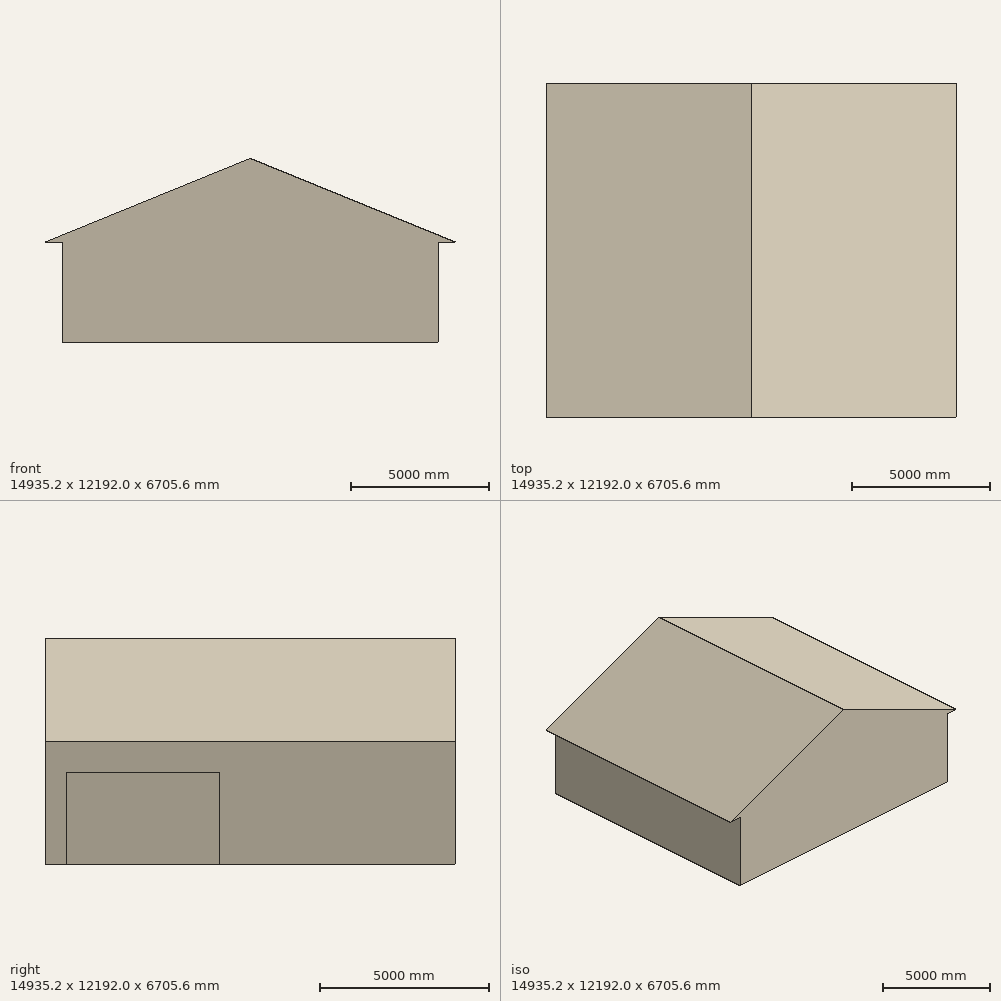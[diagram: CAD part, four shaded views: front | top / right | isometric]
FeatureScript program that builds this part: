
annotation { "Feature Type Name" : "Feature", "Feature Type Description" : "" }
export const myFeature = defineFeature(function(context is Context, id is Id, definition is map)
    precondition{}
    {
        {
            var Q0;
            Q0=qCreatedBy(makeId("Top.planeOp"),FACE);
            var sketch = newSketch(context, id + "F0", { "sketchPlane" : qUnion([Q0])});
            skLineSegment(sketch, "E0.bottom", {"start": v(6858, 6096) * mm, "end": v(-6858, 6096) * mm});
            skLineSegment(sketch, "E0.top", {"start": v(6858, -6096) * mm, "end": v(-6858, -6096) * mm});
            skLineSegment(sketch, "E0.left", {"start": v(6858, 6096) * mm, "end": v(6858, -6096) * mm});
            skLineSegment(sketch, "E0.right", {"start": v(-6858, 6096) * mm, "end": v(-6858, -6096) * mm});
            skPoint(sketch, "E0.middle", {"position": v(0, 0) * mm});
            skSolve(sketch);
        }
        {
            var Q0;
            Q0=makeQuery(id+"F0.imprint","IMPRINT",FACE,{"disambiguationData":[TD([[makeQuery(id+"F0.imprint","IMPRINT",EDGE,{"derivedFrom":sQuery(id+"F0.wireOp",EDGE,"E0.bottom")}),1.0]])]});
            extrude(context, id + "F1", {"entities" : qUnion([Q0]), "depth" : 3657.6 * mm});
        }
        {
            var Q0;
            Q0=makeQuery(id+"F1.opExtrude","SWEPT_FACE",FACE,{"disambiguationData":[OSD([sQuery(id+"F0.wireOp",EDGE,"E0.bottom")])]});
            var sketch = newSketch(context, id + "F2", { "sketchPlane" : qUnion([Q0])});
            skLineSegment(sketch, "E1", {"start": v(0, 0) * mm, "end": v(0, 2743.2) * mm});
            skPoint(sketch, "E1.endSnap0", {"position": v(0, 0) * mm});
            skLineSegment(sketch, "E2", {"start": v(0, 2743.2) * mm, "end": v(6096, 2743.2) * mm});
            skLineSegment(sketch, "E3", {"start": v(6096, 2743.2) * mm, "end": v(6096, 0) * mm});
            skSolve(sketch);
        }
        {
            var Q0;
            {var subQ0=sQuery(id+"F2.wireOp",EDGE,"E1");Q0=makeQuery(id+"F2.imprint","IMPRINT",FACE,{"disambiguationData":[TD([[makeQuery(id+"F2.imprint","IMPRINT",EDGE,{"derivedFrom":subQ0}),-1.0]])]});}
            extrude(context, id + "F3", {"entities" : qUnion([Q0]), "operationType" : NewBodyOperationType.REMOVE, "oppositeDirection" : true, "depth" : 12070.08 * mm});
        }
        {
            var Q0;
            Q0=makeQuery(id+"F1.opExtrude","SWEPT_FACE",FACE,{"disambiguationData":[OSD([sQuery(id+"F0.wireOp",EDGE,"E0.left")])]});
            var sketch = newSketch(context, id + "F4", { "sketchPlane" : qUnion([Q0])});
            skPoint(sketch, "E4.endSnap0", {"position": v(-914.4, 0) * mm});
            skLineSegment(sketch, "E5", {"start": v(-914.4, 2743.2) * mm, "end": v(-5486.4, 2743.2) * mm});
            skLineSegment(sketch, "E6", {"start": v(-5486.4, 2743.2) * mm, "end": v(-5486.4, 0) * mm});
            skLineSegment(sketch, "E7", {"start": v(-914.4, 2743.2) * mm, "end": v(-914.4, 0) * mm});
            skSolve(sketch);
        }
        {
            var Q0;
            Q0 = qSketchRegion(id + "F4", true);
            var Q1;
            Q1=makeQuery(id+"F4.imprint","IMPRINT",FACE,{"disambiguationData":[TD([[makeQuery(id+"F4.imprint","IMPRINT",EDGE,{"derivedFrom":sQuery(id+"F4.wireOp",EDGE,"E5")}),1.0]])]});
            extrude(context, id + "F5", {"entities" : qUnion([Q0, Q1]), "operationType" : NewBodyOperationType.REMOVE, "oppositeDirection" : true, "depth" : 13594.08 * mm});
        }
        {
            var Q0;
            {var subQ0=sQuery(id+"F0.wireOp",EDGE,"E0.left");Q0=makeQuery(id+"F5.boolean.opBoolean","COPY",FACE,{"disambiguationData":[TD([makeQuery(id+"F1.opExtrude","SWEPT_FACE",FACE,{"disambiguationData":[OSD([subQ0])]})])],"derivedFrom":makeQuery(id+"F5.opExtrude","SWEPT_FACE",FACE,{"disambiguationData":[OSD([sQuery(id+"F4.wireOp",EDGE,"E6")])]})});}
            var sketch = newSketch(context, id + "F6", { "sketchPlane" : qUnion([Q0])});
            skLineSegment(sketch, "E8", {"start": v(0, 2743.2) * mm, "end": v(0, 0) * mm});
            skLineSegment(sketch, "E9", {"start": v(0, 0) * mm, "end": v(-6675.12, 0) * mm});
            skLineSegment(sketch, "E10", {"start": v(-6675.12, 0) * mm, "end": v(-6675.12, 2743.2) * mm});
            skLineSegment(sketch, "E11", {"start": v(-6675.12, 2743.2) * mm, "end": v(0, 2743.2) * mm});
            skSolve(sketch);
        }
        {
            var Q0;
            Q0=makeQuery(id+"F6.imprint","IMPRINT",FACE,{"disambiguationData":[TD([[makeQuery(id+"F6.imprint","IMPRINT",EDGE,{"derivedFrom":sQuery(id+"F6.wireOp",EDGE,"E8")}),1.0]])]});
            extrude(context, id + "F7", {"entities" : qUnion([Q0]), "operationType" : NewBodyOperationType.REMOVE, "oppositeDirection" : true, "depth" : 487.68 * mm});
        }
        {
            var Q0;
            {var subQ0=sQuery(id+"F0.wireOp",EDGE,"E0.bottom");var subQ1=sQuery(id+"F0.wireOp",EDGE,"E0.left");Q0=makeQuery(id+"F5.boolean.opBoolean","SPLIT",FACE,{"disambiguationData":[TD([makeQuery(id+"F1.opExtrude","SWEPT_FACE",FACE,{"disambiguationData":[OSD([subQ0])]}),makeQuery(id+"F1.opExtrude","SWEPT_FACE",FACE,{"disambiguationData":[OSD([subQ1])]}),makeQuery(id+"F3.boolean.opBoolean","COPY",FACE,{"derivedFrom":makeQuery(id+"F3.opExtrude","SWEPT_FACE",FACE,{"disambiguationData":[OSD([sQuery(id+"F2.wireOp",EDGE,"E1")])]})}),makeQuery(id+"F5.opExtrude","SWEPT_FACE",FACE,{"disambiguationData":[OSD([sQuery(id+"F4.wireOp",EDGE,"E7")])]})])],"derivedFrom":makeQuery(id+"F1.opExtrude","CAP_FACE",FACE,{"disambiguationData":[OSD([subQ0,sQuery(id+"F0.wireOp",EDGE,"E0.top"),subQ1,sQuery(id+"F0.wireOp",EDGE,"E0.right")])],"isStart":true})});}
            var sketch = newSketch(context, id + "F8", { "sketchPlane" : qUnion([Q0])});
            skLineSegment(sketch, "E12", {"start": v(0, 914.4) * mm, "end": v(0, -5913.12) * mm});
            skLineSegment(sketch, "E13", {"start": v(0, -5913.12) * mm, "end": v(6675.12, -5913.12) * mm});
            skLineSegment(sketch, "E14", {"start": v(6675.12, -5913.12) * mm, "end": v(6675.12, 914.4) * mm});
            skLineSegment(sketch, "E15", {"start": v(6675.12, 914.4) * mm, "end": v(0, 914.4) * mm});
            skSolve(sketch);
        }
        {
            var Q0;
            Q0=makeQuery(id+"F8.imprint","IMPRINT",FACE,{"disambiguationData":[TD([[makeQuery(id+"F8.imprint","IMPRINT",EDGE,{"derivedFrom":sQuery(id+"F8.wireOp",EDGE,"E12")}),1.0]])]});
            extrude(context, id + "F9", {"entities" : qUnion([Q0]), "operationType" : NewBodyOperationType.REMOVE, "oppositeDirection" : true, "depth" : 3657.6 * mm});
        }
        {
            var Q0;
            Q0=makeQuery(id+"F1.opExtrude","SWEPT_FACE",FACE,{"disambiguationData":[OSD([sQuery(id+"F0.wireOp",EDGE,"E0.top")])]});
            var sketch = newSketch(context, id + "F10", { "sketchPlane" : qUnion([Q0])});
            skLineSegment(sketch, "E16", {"start": v(0, 3657.6) * mm, "end": v(0, 6705.6) * mm, "construction": true});
            skPoint(sketch, "E16.endSnap0", {"position": v(0, 3657.6) * mm});
            skLineSegment(sketch, "E17", {"start": v(6858, 3657.6) * mm, "end": v(7467.6, 3657.6) * mm});
            skLineSegment(sketch, "E18", {"start": v(-6858, 3657.6) * mm, "end": v(-7467.6, 3657.6) * mm});
            skLineSegment(sketch, "E19", {"start": v(-7467.6, 3657.6) * mm, "end": v(0, 6705.6) * mm});
            skLineSegment(sketch, "E20", {"start": v(0, 6705.6) * mm, "end": v(7467.6, 3657.6) * mm});
            skSolve(sketch);
        }
        {
            var Q0;
            Q0=makeQuery(id+"F1.opExtrude","CAP_FACE",FACE,{"disambiguationData":[OSD([sQuery(id+"F0.wireOp",EDGE,"E0.bottom"),sQuery(id+"F0.wireOp",EDGE,"E0.top"),sQuery(id+"F0.wireOp",EDGE,"E0.left"),sQuery(id+"F0.wireOp",EDGE,"E0.right")])],"isStart":false});
            var sketch = newSketch(context, id + "F11", { "sketchPlane" : qUnion([Q0])});
            skLineSegment(sketch, "E21", {"start": v(6675.12, -914.4) * mm, "end": v(6675.12, -5913.12) * mm});
            skLineSegment(sketch, "E22", {"start": v(6675.12, -5913.12) * mm, "end": v(-6675.12, -5913.12) * mm});
            skLineSegment(sketch, "E23", {"start": v(-6675.12, -5913.12) * mm, "end": v(-6675.12, 5913.12) * mm});
            skLineSegment(sketch, "E24", {"start": v(-6675.12, 5913.12) * mm, "end": v(0, 5913.12) * mm});
            skSolve(sketch);
        }
        {
            var Q0;
            Q0 = qSketchRegion(id + "F11", true);
            var Q1;
            Q1=makeQuery(id+"F11.imprint","IMPRINT",FACE,{"disambiguationData":[TD([[makeQuery(id+"F11.imprint","IMPRINT",EDGE,{"derivedFrom":sQuery(id+"F11.wireOp",EDGE,"E21")}),-1.0]])]});
            extrude(context, id + "F12", {"entities" : qUnion([Q0, Q1]), "operationType" : NewBodyOperationType.REMOVE, "endBound" : BoundingType.THROUGH_ALL, "oppositeDirection" : true, "depth" : 30.48 * mm});
        }
        {
            var Q0;
            Q0 = qSketchRegion(id + "F10", true);
            var Q1;
            Q1=makeQuery(id+"F10.imprint","IMPRINT",FACE,{"disambiguationData":[TD([[makeQuery(id+"F10.imprint","IMPRINT",EDGE,{"derivedFrom":sQuery(id+"F10.wireOp",EDGE,"E17")}),1.0]])]});
            extrude(context, id + "F13", {"entities" : qUnion([Q0, Q1]), "operationType" : NewBodyOperationType.ADD, "oppositeDirection" : true, "depth" : 12192 * mm});
        }
        {
            var Q0;
            Q0=makeQuery(id+"F7.boolean.opBoolean","MERGE",FACE,{"derivedFrom":[makeQuery(id+"F3.boolean.opBoolean","COPY",FACE,{"derivedFrom":makeQuery(id+"F3.opExtrude","CAP_FACE",FACE,{"disambiguationData":[OSD([sQuery(id+"F0.wireOp",EDGE,"E0.bottom"),sQuery(id+"F2.wireOp",EDGE,"E1"),sQuery(id+"F2.wireOp",EDGE,"E2"),sQuery(id+"F2.wireOp",EDGE,"E3")])],"isStart":false})}),makeQuery(id+"F7.opExtrude","CAP_FACE",FACE,{"disambiguationData":[OSD([sQuery(id+"F6.wireOp",EDGE,"E8"),sQuery(id+"F6.wireOp",EDGE,"E9"),sQuery(id+"F6.wireOp",EDGE,"E10"),sQuery(id+"F6.wireOp",EDGE,"E11")])],"isStart":false})]});
            extrude(context, id + "F14", {"entities" : qUnion([Q0]), "operationType" : NewBodyOperationType.ADD, "depth" : 60.96 * mm});
        }
        {
            var Q0;
            Q0=makeQuery(id+"F5.boolean.opBoolean","COPY",FACE,{"derivedFrom":makeQuery(id+"F5.opExtrude","CAP_FACE",FACE,{"disambiguationData":[OSD([sQuery(id+"F0.wireOp",EDGE,"E0.left"),sQuery(id+"F4.wireOp",EDGE,"E5"),sQuery(id+"F4.wireOp",EDGE,"E6"),sQuery(id+"F4.wireOp",EDGE,"E7")])],"isStart":false})});
            extrude(context, id + "F15", {"entities" : qUnion([Q0]), "operationType" : NewBodyOperationType.ADD, "depth" : 60.96 * mm});
        }
    });
